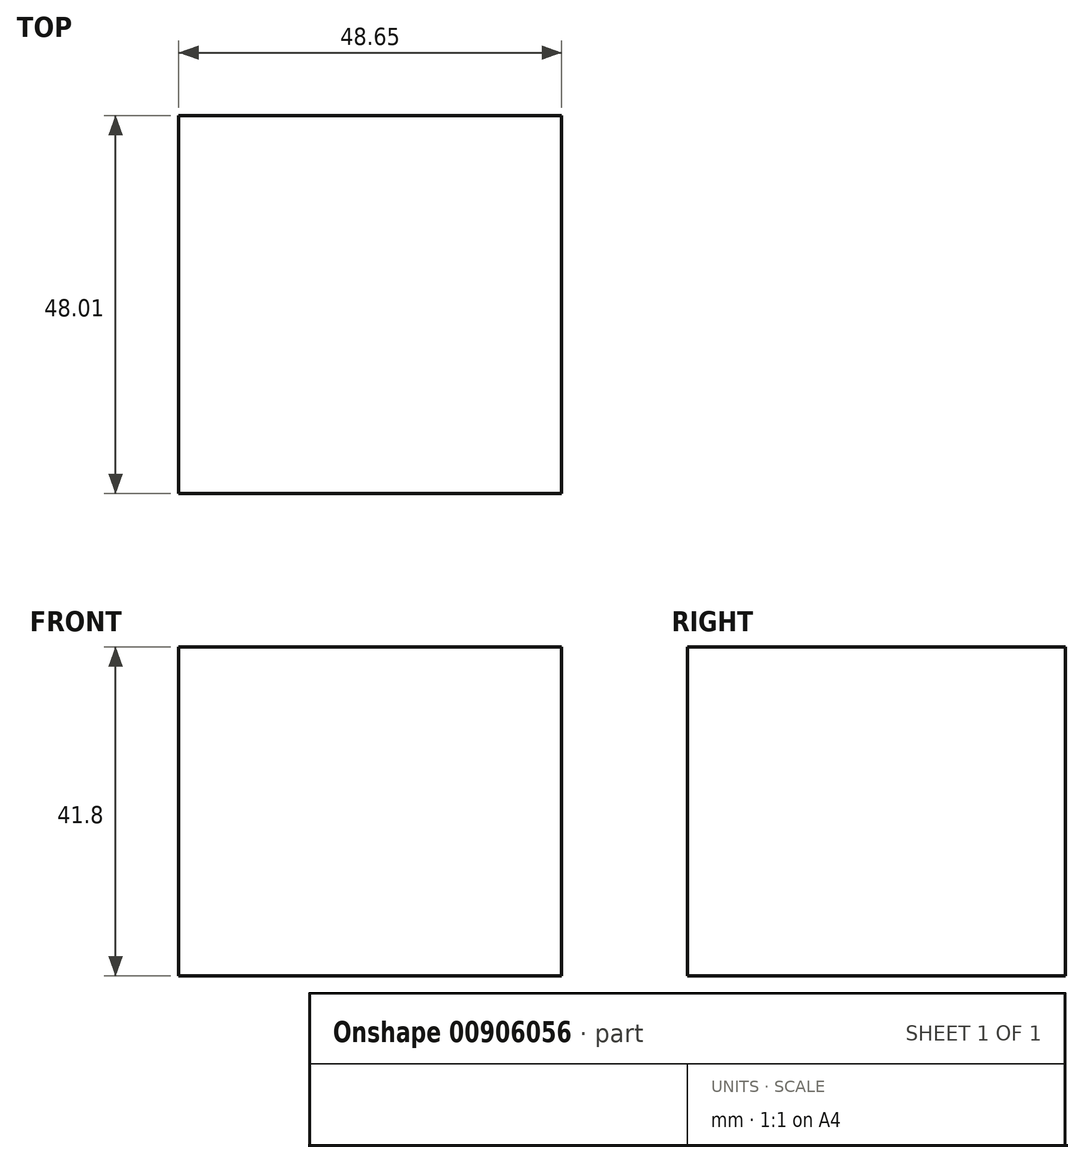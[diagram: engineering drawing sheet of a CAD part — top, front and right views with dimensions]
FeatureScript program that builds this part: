
annotation { "Feature Type Name" : "Feature", "Feature Type Description" : "" }
export const myFeature = defineFeature(function(context is Context, id is Id, definition is map)
    precondition{}
    {
        {
            var Q0;
            Q0=qCreatedBy(makeId("Front.planeOp"),FACE);
            var sketch = newSketch(context, id + "F0", { "sketchPlane" : qUnion([Q0])});
            skLineSegment(sketch, "E0.bottom", {"start": v(-41.58, -6.45) * mm, "end": v(7.07, -6.45) * mm});
            skLineSegment(sketch, "E0.top", {"start": v(-41.58, -48.25) * mm, "end": v(7.07, -48.25) * mm});
            skLineSegment(sketch, "E0.left", {"start": v(-41.58, -6.45) * mm, "end": v(-41.58, -48.25) * mm});
            skLineSegment(sketch, "E0.right", {"start": v(7.07, -6.45) * mm, "end": v(7.07, -48.25) * mm});
            skSolve(sketch);
        }
        {
            var Q0;
            Q0 = qSketchRegion(id + "F0", true);
            extrude(context, id + "F1", {"entities" : qUnion([Q0]), "oppositeDirection" : true, "depth" : 48 * mm, "offsetDistance" : 25.4 * mm});
        }
    });
